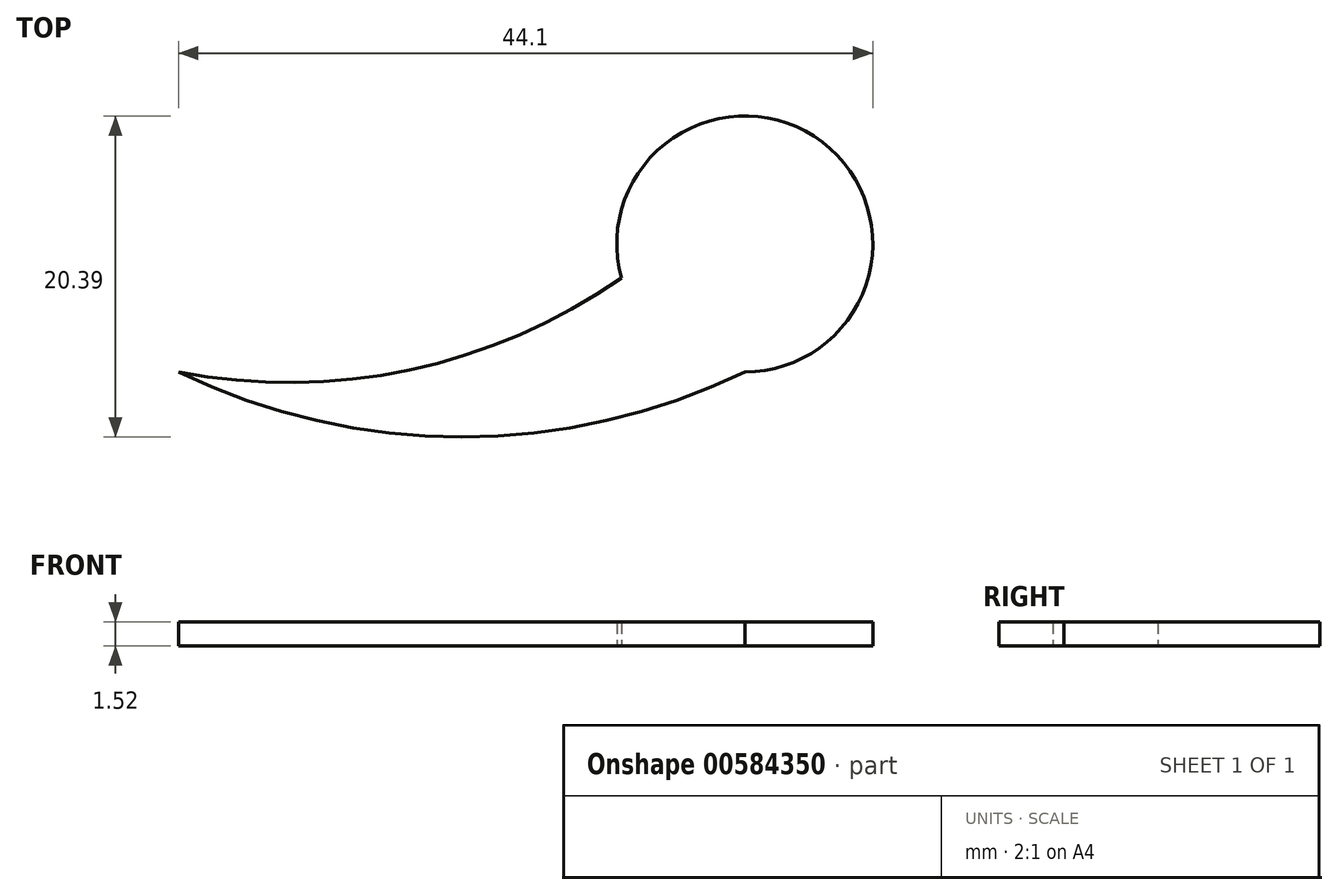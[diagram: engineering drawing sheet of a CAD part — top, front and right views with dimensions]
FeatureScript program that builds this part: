
annotation { "Feature Type Name" : "Feature", "Feature Type Description" : "" }
export const myFeature = defineFeature(function(context is Context, id is Id, definition is map)
    precondition{}
    {
        {
            var Q0;
            Q0=qCreatedBy(makeId("Top.planeOp"),FACE);
            var sketch = newSketch(context, id + "F0", { "sketchPlane" : qUnion([Q0])});
            skArc(sketch, "E0", {"start": v(-35.97, 0) * mm, "mid": v(-17.99, -4.13) * mm, "end": v(0, 0) * mm});
            skArc(sketch, "E1", {"start": v(0, 0) * mm, "mid": v(4.93, 14.6) * mm, "end": v(-7.84, 5.97) * mm});
            skArc(sketch, "E2", {"start": v(-35.97, 0) * mm, "mid": v(-21.3, 0.13) * mm, "end": v(-7.84, 5.97) * mm});
            skSolve(sketch);
        }
        {
            var Q0;
            Q0=makeQuery(id+"F0.imprint","IMPRINT",FACE,{"disambiguationData":[TD([[makeQuery(id+"F0.imprint","IMPRINT",EDGE,{"derivedFrom":sQuery(id+"F0.wireOp",EDGE,"E0")}),1.0]])]});
            extrude(context, id + "F1", {"entities" : qUnion([Q0]), "depth" : 1.52 * mm, "offsetDistance" : 25.4 * mm});
        }
    });
